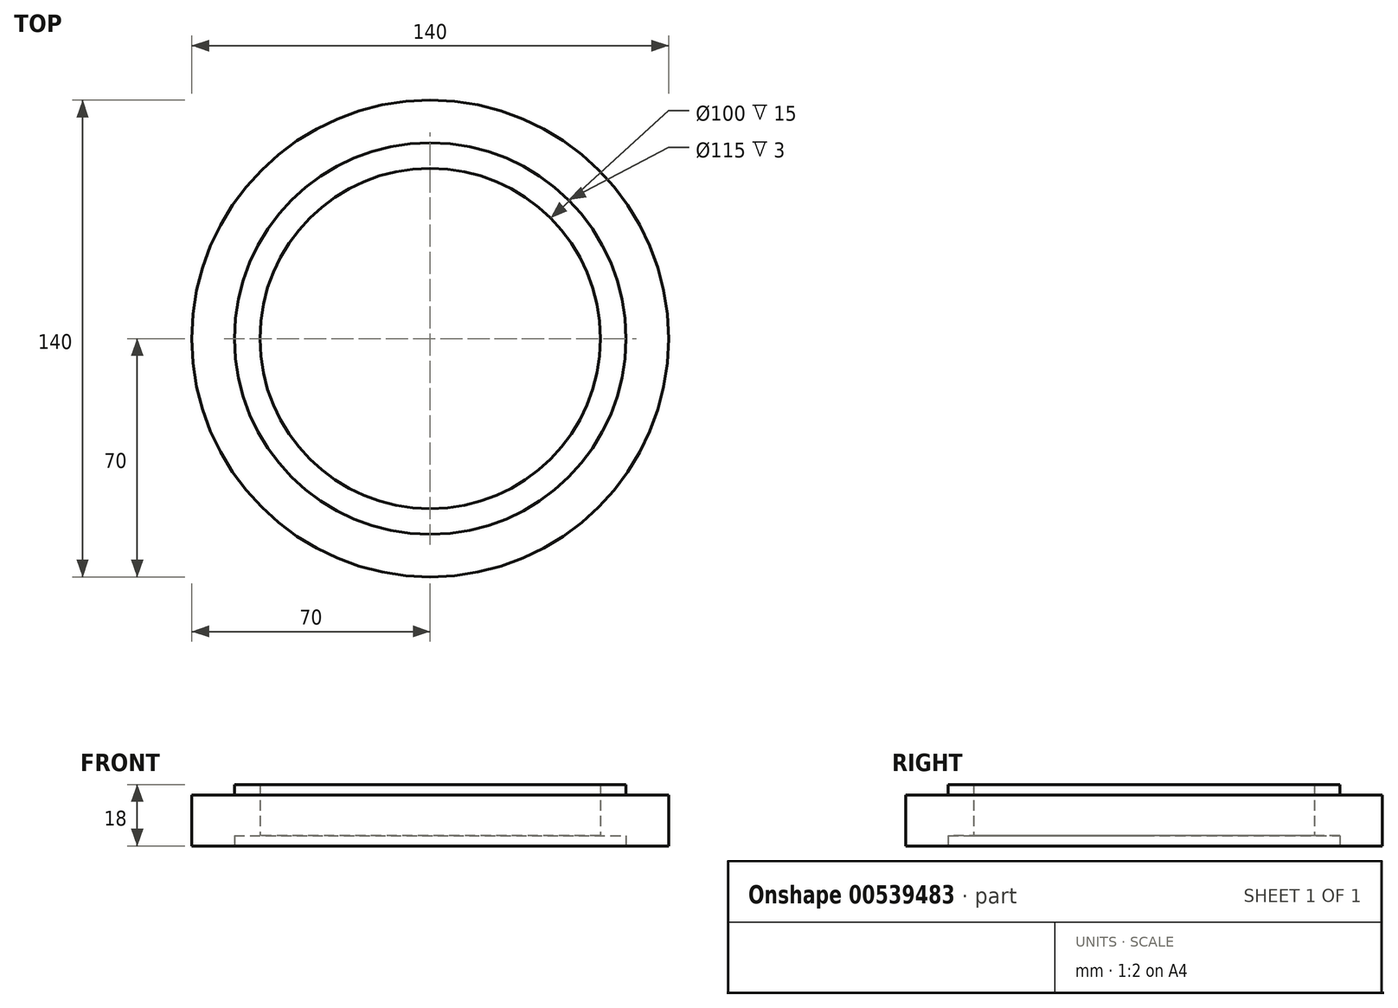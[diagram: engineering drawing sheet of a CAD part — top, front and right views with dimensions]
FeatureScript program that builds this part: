
annotation { "Feature Type Name" : "Feature", "Feature Type Description" : "" }
export const myFeature = defineFeature(function(context is Context, id is Id, definition is map)
    precondition{}
    {
        {
            var Q0;
            Q0=qCreatedBy(makeId("Top.planeOp"),FACE);
            var sketch = newSketch(context, id + "F0", { "sketchPlane" : qUnion([Q0])});
            skCircle(sketch, "E0", {"center": v(0, 0) * mm, "radius": 70 * mm});
            skCircle(sketch, "E1", {"center": v(0, 0) * mm, "radius": 50 * mm});
            skSolve(sketch);
        }
        {
            var Q0;
            Q0=makeQuery(id+"F0.imprint","IMPRINT",FACE,{"disambiguationData":[TD([[makeQuery(id+"F0.imprint","IMPRINT",EDGE,{"derivedFrom":sQuery(id+"F0.wireOp",EDGE,"E0")}),1.0]])]});
            extrude(context, id + "F1", {"entities" : qUnion([Q0]), "depth" : 15 * mm, "offsetDistance" : 25 * mm});
        }
        {
            var Q0;
            Q0=makeQuery(id+"F1.opExtrude","CAP_FACE",FACE,{"disambiguationData":[OSD([sQuery(id+"F0.wireOp",EDGE,"E0"),sQuery(id+"F0.wireOp",EDGE,"E1")])],"isStart":false});
            var sketch = newSketch(context, id + "F2", { "sketchPlane" : qUnion([Q0])});
            skSolve(sketch);
        }
        {
            var Q0;
            Q0=makeQuery(id+"F2.imprint","IMPRINT",FACE,{"disambiguationData":[TD([[makeQuery(id+"F2.imprint","IMPRINT",EDGE,{"derivedFrom":makeQuery(id+"F1.opExtrude","CAP_EDGE",EDGE,{"disambiguationData":[OSD([sQuery(id+"F0.wireOp",EDGE,"E0")])],"isStart":false})}),1.0]])]});
            var sketch = newSketch(context, id + "F3", { "sketchPlane" : qUnion([Q0])});
            skCircle(sketch, "E2", {"center": v(0, 0) * mm, "radius": 57.5 * mm});
            skSolve(sketch);
        }
        {
            var Q0;
            Q0=makeQuery(id+"F3.imprint","IMPRINT",FACE,{"disambiguationData":[TD([[makeQuery(id+"F3.imprint","IMPRINT",EDGE,{"derivedFrom":sQuery(id+"F3.wireOp",EDGE,"E2")}),1.0]])]});
            extrude(context, id + "F4", {"entities" : qUnion([Q0]), "operationType" : NewBodyOperationType.ADD, "depth" : 3 * mm, "offsetDistance" : 25 * mm});
        }
        {
            var Q0;
            Q0=makeQuery(id+"F1.opExtrude","CAP_FACE",FACE,{"disambiguationData":[OSD([sQuery(id+"F0.wireOp",EDGE,"E0"),sQuery(id+"F0.wireOp",EDGE,"E1")])],"isStart":true});
            var sketch = newSketch(context, id + "F5", { "sketchPlane" : qUnion([Q0])});
            skCircle(sketch, "E3", {"center": v(0, 0) * mm, "radius": 57.5 * mm});
            skSolve(sketch);
        }
        {
            var Q0;
            Q0=makeQuery(id+"F5.imprint","IMPRINT",FACE,{"disambiguationData":[TD([[makeQuery(id+"F5.imprint","IMPRINT",EDGE,{"derivedFrom":sQuery(id+"F5.wireOp",EDGE,"E3")}),1.0]])]});
            extrude(context, id + "F6", {"entities" : qUnion([Q0]), "operationType" : NewBodyOperationType.REMOVE, "oppositeDirection" : true, "depth" : 3 * mm, "offsetDistance" : 25 * mm});
        }
    });
